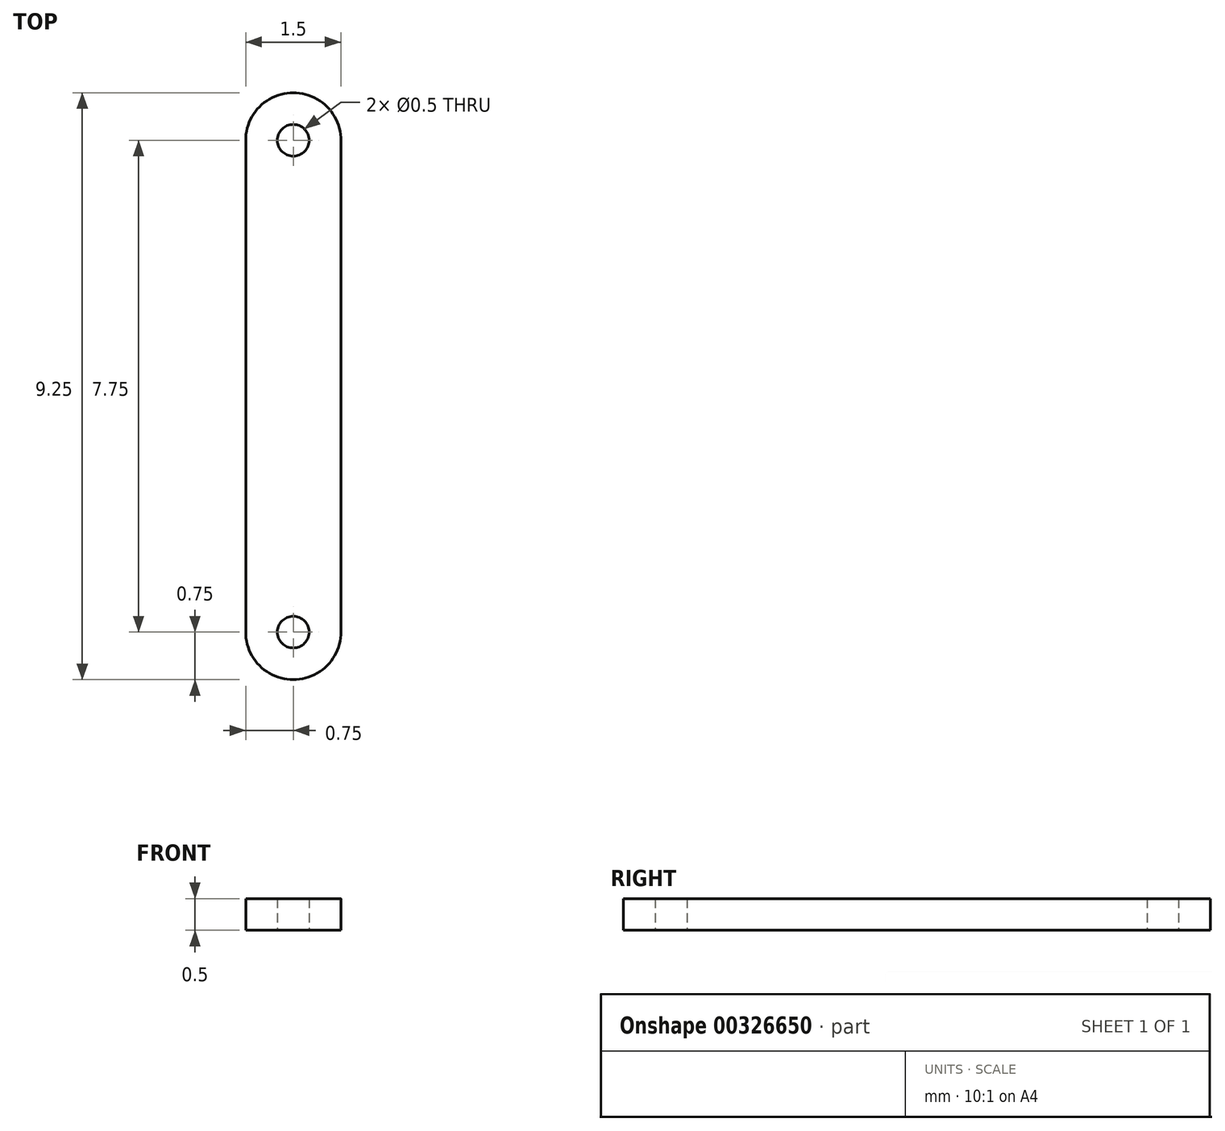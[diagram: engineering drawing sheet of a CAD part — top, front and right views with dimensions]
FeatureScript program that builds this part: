
annotation { "Feature Type Name" : "Feature", "Feature Type Description" : "" }
export const myFeature = defineFeature(function(context is Context, id is Id, definition is map)
    precondition{}
    {
        {
            var Q0;
            Q0=qCreatedBy(makeId("Top.planeOp"),FACE);
            var sketch = newSketch(context, id + "F0", { "sketchPlane" : qUnion([Q0])});
            skArc(sketch, "E0", {"start": v(0.75, 37.43) * mm, "mid": v(0, 38.19) * mm, "end": v(-0.75, 37.43) * mm});
            skArc(sketch, "E1", {"start": v(-0.75, 29.7) * mm, "mid": v(0, 28.94) * mm, "end": v(0.75, 29.7) * mm});
            skCircle(sketch, "E2", {"center": v(0, 37.44) * mm, "radius": 0.25 * mm});
            skCircle(sketch, "E3", {"center": v(0, 29.69) * mm, "radius": 0.25 * mm});
            skLineSegment(sketch, "E4", {"start": v(-0.75, 37.44) * mm, "end": v(-0.75, 29.68) * mm});
            skLineSegment(sketch, "E5", {"start": v(0.75, 29.68) * mm, "end": v(0.75, 37.44) * mm});
            skSolve(sketch);
        }
        {
            var Q0;
            {var subQ1=sQuery(id+"F0.wireOp",EDGE,"E0");Q0=makeQuery(id+"F0.imprint","IMPRINT",FACE,{"disambiguationData":[TD([[makeQuery(id+"F0.imprint","IMPRINT",EDGE,{"derivedFrom":subQ1}),1.0]])]});}
            extrude(context, id + "F1", {"entities" : qUnion([Q0]), "depth" : .5 * mm});
        }
    });
